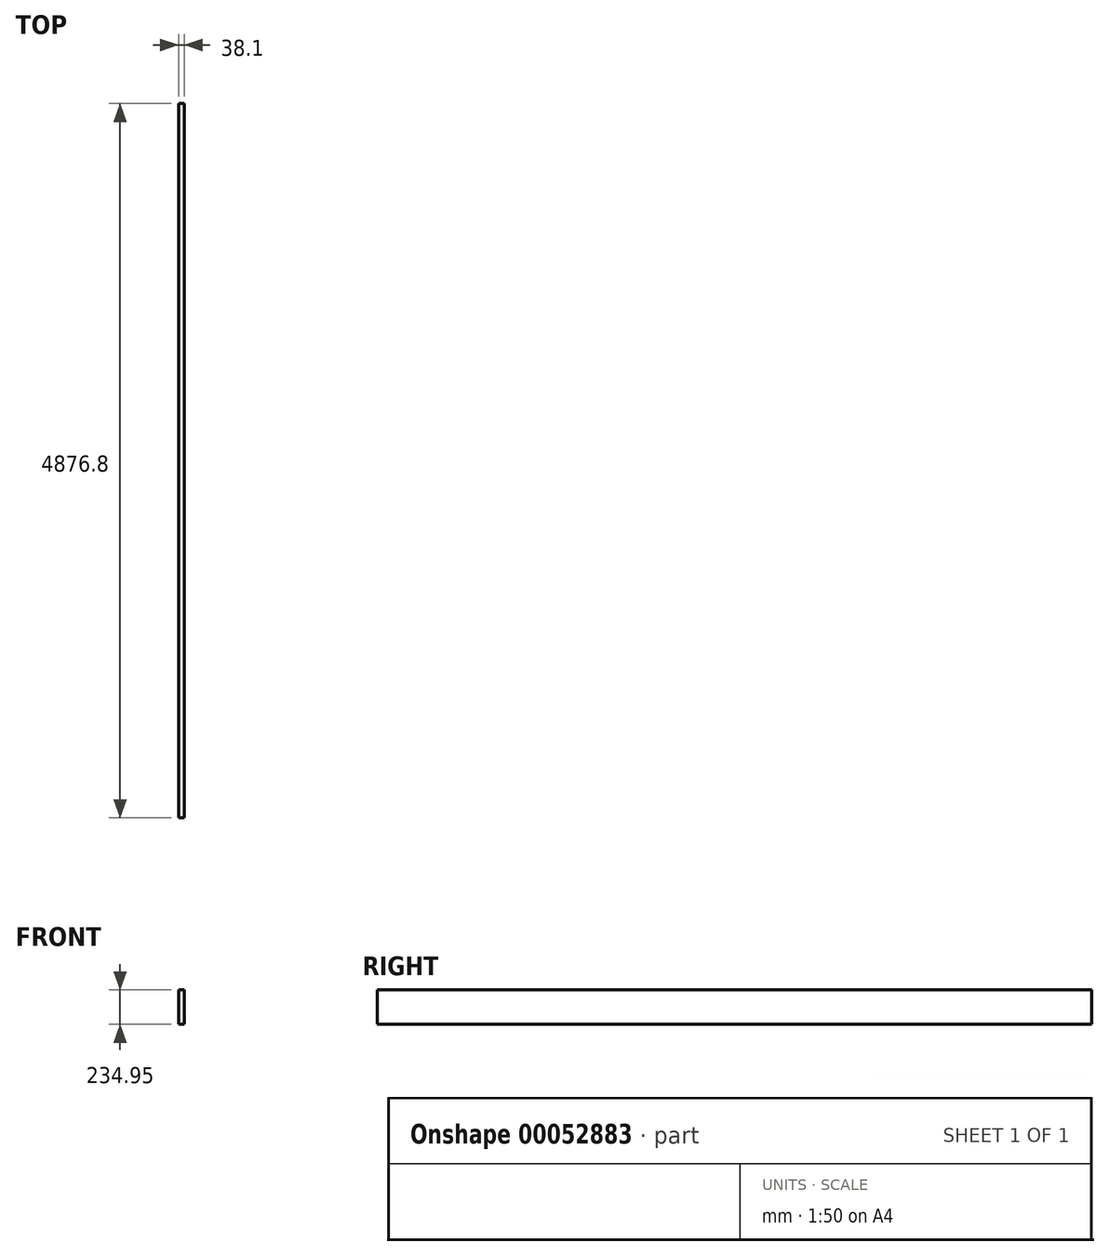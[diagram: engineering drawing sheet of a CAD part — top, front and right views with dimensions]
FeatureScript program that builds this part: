
annotation { "Feature Type Name" : "Feature", "Feature Type Description" : "" }
export const myFeature = defineFeature(function(context is Context, id is Id, definition is map)
    precondition{}
    {
        {
            var Q0;
            Q0=qCreatedBy(makeId("Front.planeOp"),FACE);
            var sketch = newSketch(context, id + "F0", { "sketchPlane" : qUnion([Q0])});
            skLineSegment(sketch, "E0.bottom", {"start": v(0, 0) * mm, "end": v(38.1, 0) * mm});
            skLineSegment(sketch, "E0.top", {"start": v(0, -234.95) * mm, "end": v(38.1, -234.95) * mm});
            skLineSegment(sketch, "E0.left", {"start": v(0, 0) * mm, "end": v(0, -234.95) * mm});
            skLineSegment(sketch, "E0.right", {"start": v(38.1, 0) * mm, "end": v(38.1, -234.95) * mm});
            skSolve(sketch);
        }
        {
            var Q0;
            Q0=qSketchRegion(id+"F0",true);
            extrude(context, id + "F1", {"entities" : qUnion([Q0]), "depth" : 4876.8 * mm});
        }
    });
